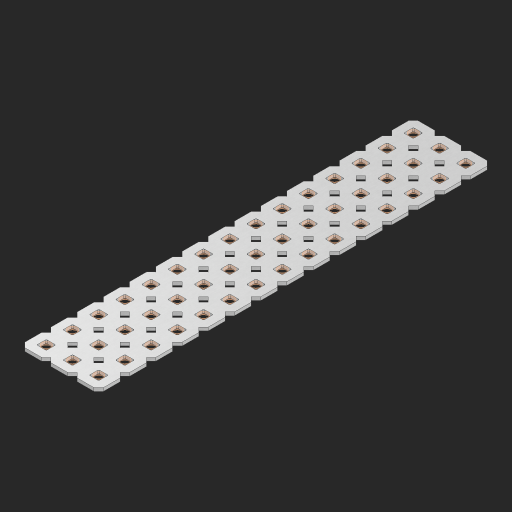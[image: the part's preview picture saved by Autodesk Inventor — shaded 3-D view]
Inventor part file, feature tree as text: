
AUTODESK INVENTOR PART (.ipt)
format: ipt  version: 2023 (Build 270158000, 158)  size: 800,768 bytes
history: native  units: in
note: dims shown in document units (in); Inventor stores cm internally (conversion verified against a paired STEP export)
features: other x46, extrude x44, sketch x2, pattern_linear x1
ambient origin geometry x8: Origin, YZ Plane, XZ Plane, XY Plane, X Axis, Y Axis, Z Axis, Center Point
bodies: Solid1 (feature_tree), Body (feature_tree)
feature tree (93):
  pattern_linear  "Rectangular Pattern1"  Spacing1=0.09in  [1 undecoded]
  sketch  "Sketch1"  dims[d1=0.5in]
  sketch  "Sketch2"  dims[d2=0.182in d3=0.09in d4=0.09in d5=0.09in d6=0.09in d7=0.09in d8=0.09in d9=0.09in d10=0.09in d11=0.02in d13=0.0in d14=0.172in d15=0.0625in d16=0.0in d19=0.5in d22=0.5in]
  other  "Srf1"
  other  "Srf126"
  other  "Srf127"
  other  "Srf128"
  other  "Srf129"
  other  "Srf130"
  other  "Srf131"
  other  "Srf250"
  other  "Srf251"
  other  "Srf252"
  other  "Srf253"
  other  "Srf254"
  other  "Srf255"
  other  "Srf256"
  other  "Srf257"
  other  "Srf268"
  other  "Srf269"
  other  "Srf270"
  other  "Srf271"
  other  "Srf272"
  other  "Srf273"
  other  "Srf274"
  other  "Srf275"
  other  "Srf276"
  other  "Srf277"
  other  "Srf278"
  other  "Srf279"
  other  "Srf280"
  other  "Srf281"
  other  "Srf282"
  other  "Srf293"
  other  "Srf294"
  other  "Srf295"
  other  "Srf296"
  other  "Srf297"
  other  "Srf298"
  other  "Srf299"
  other  "Srf300"
  other  "Srf301"
  other  "Srf302"
  other  "Srf303"
  other  "Srf304"
  other  "Srf305"
  other  "Srf306"
  other  "Srf307"
  other  "Circle"
  extrude  "ExtrusionSrf126"  Depth=0.09in
  extrude  "ExtrusionSrf127"  Depth=0.09in
  extrude  "ExtrusionSrf128"  Depth=0.09in
  extrude  "ExtrusionSrf129"  Depth=0.09in
  extrude  "ExtrusionSrf130"  Depth=0.09in
  extrude  "ExtrusionSrf131"  Depth=0.09in
  extrude  "ExtrusionSrf250"  Depth=0.09in
  extrude  "ExtrusionSrf251"  Depth=0.02in
  extrude  "ExtrusionSrf252"  TaperAngle=0.0deg  [1 undecoded]
  extrude  "ExtrusionSrf253"  Depth=0.5in
  extrude  "ExtrusionSrf254"  Depth=0.0625in TaperAngle=0.0deg
  extrude  "ExtrusionSrf255"  Depth=0.5in
  extrude  "ExtrusionSrf256"  Depth=0.5in
  extrude  "ExtrusionSrf257"  [1 undecoded]
  extrude  "ExtrusionSrf268"  [1 undecoded]
  extrude  "ExtrusionSrf269"  [1 undecoded]
  extrude  "ExtrusionSrf270"  [1 undecoded]
  extrude  "ExtrusionSrf271"  [1 undecoded]
  extrude  "ExtrusionSrf272"  [1 undecoded]
  extrude  "ExtrusionSrf273"  [1 undecoded]
  extrude  "ExtrusionSrf274"  [1 undecoded]
  extrude  "ExtrusionSrf275"  [1 undecoded]
  extrude  "ExtrusionSrf276"  [1 undecoded]
  extrude  "ExtrusionSrf277"  [1 undecoded]
  extrude  "ExtrusionSrf278"  [1 undecoded]
  extrude  "ExtrusionSrf279"  [1 undecoded]
  extrude  "ExtrusionSrf280"  [1 undecoded]
  extrude  "ExtrusionSrf281"  [1 undecoded]
  extrude  "ExtrusionSrf282"  [1 undecoded]
  extrude  "ExtrusionSrf293"  [1 undecoded]
  extrude  "ExtrusionSrf294"  [1 undecoded]
  extrude  "ExtrusionSrf295"  [1 undecoded]
  extrude  "ExtrusionSrf296"  [1 undecoded]
  extrude  "ExtrusionSrf297"  [1 undecoded]
  extrude  "ExtrusionSrf298"  [1 undecoded]
  extrude  "ExtrusionSrf299"  [1 undecoded]
  extrude  "ExtrusionSrf300"  [1 undecoded]
  extrude  "ExtrusionSrf301"  [1 undecoded]
  extrude  "ExtrusionSrf302"  [1 undecoded]
  extrude  "ExtrusionSrf303"  [1 undecoded]
  extrude  "ExtrusionSrf304"  [1 undecoded]
  extrude  "ExtrusionSrf305"  [1 undecoded]
  extrude  "ExtrusionSrf306"  [1 undecoded]
  extrude  "ExtrusionSrf307"  [1 undecoded]
note: 33 required parameter values undecoded (feature->parameter linkage not recoverable at this tier; creation-order binding heuristic only, values carry confidence <= 0.55)
